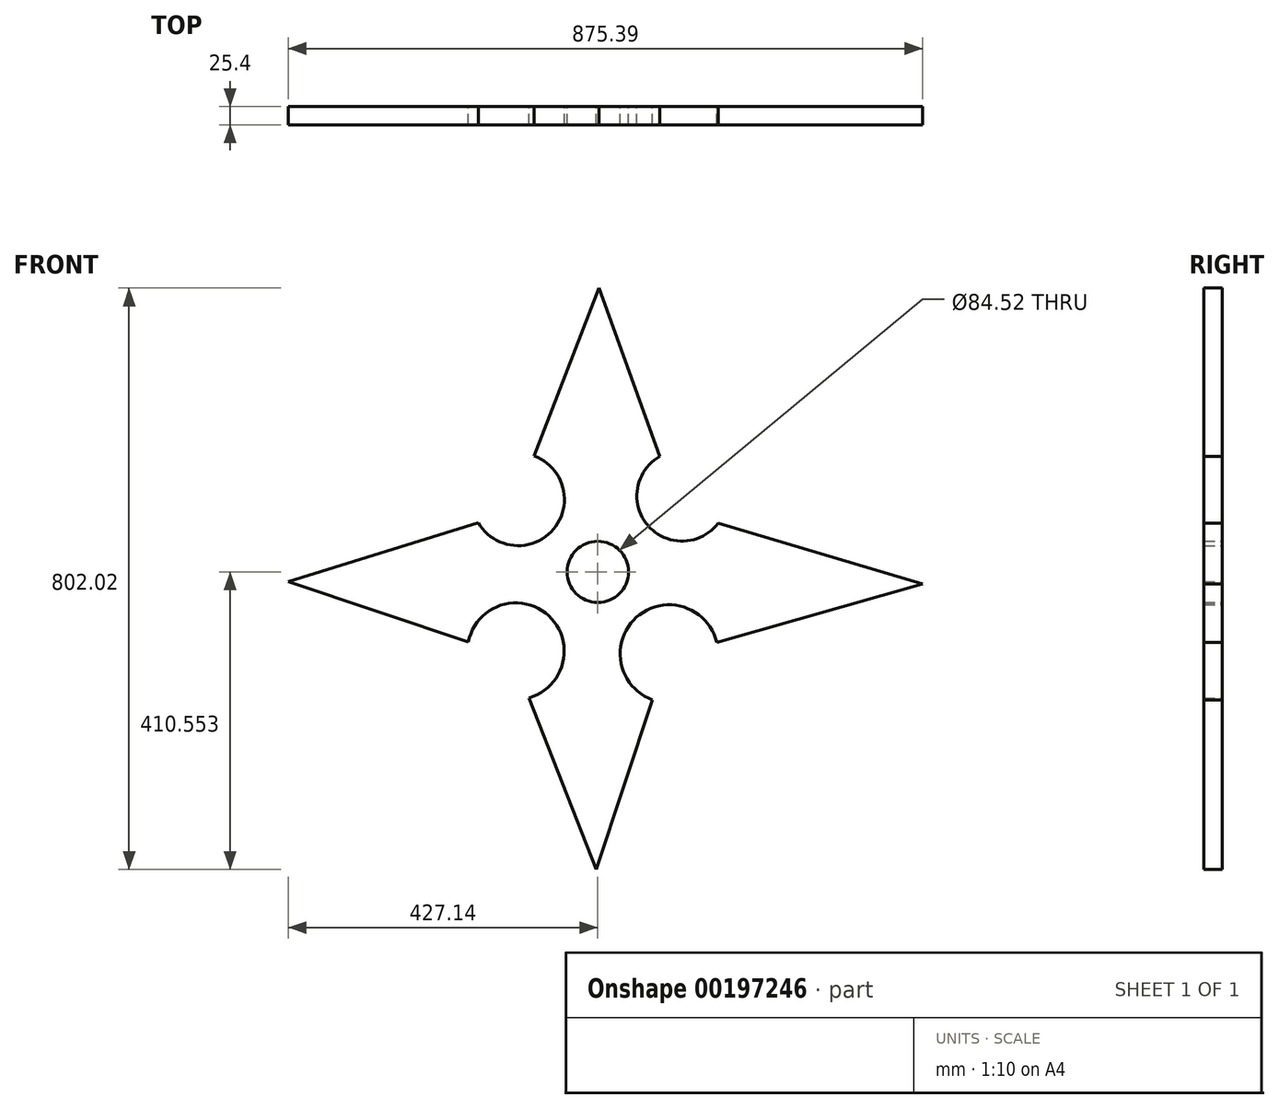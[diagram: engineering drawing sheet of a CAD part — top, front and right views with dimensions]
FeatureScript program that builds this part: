
annotation { "Feature Type Name" : "Feature", "Feature Type Description" : "" }
export const myFeature = defineFeature(function(context is Context, id is Id, definition is map)
    precondition{}
    {
        {
            var Q0;
            Q0=qCreatedBy(makeId("Front.planeOp"),FACE);
            var sketch = newSketch(context, id + "F0", { "sketchPlane" : qUnion([Q0])});
            skLineSegment(sketch, "E0", {"start": v(29.66, 76.77) * mm, "end": v(119.17, 308.51) * mm});
            skLineSegment(sketch, "E1", {"start": v(119.17, 308.51) * mm, "end": v(202.9, 76.26) * mm});
            skLineSegment(sketch, "E2", {"start": v(-47.67, -14.87) * mm, "end": v(-309.84, -96.66) * mm});
            skLineSegment(sketch, "E3", {"start": v(-309.84, -96.66) * mm, "end": v(-61.25, -179.52) * mm});
            skLineSegment(sketch, "E4", {"start": v(22.23, -256.74) * mm, "end": v(119.17, -504.48) * mm});
            skLineSegment(sketch, "E5", {"start": v(111.22, -504.48) * mm, "end": v(192.9, -259.48) * mm});
            skLineSegment(sketch, "E6", {"start": v(281.45, -180.33) * mm, "end": v(574.65, -96.66) * mm});
            skLineSegment(sketch, "E7", {"start": v(574.65, -101.95) * mm, "end": v(283.35, -15.69) * mm});
            skPoint(sketch, "E8", {"position": v(283.35, 59.58) * mm});
            skArc(sketch, "E9", {"start": v(202.9, 76.26) * mm, "mid": v(186.65, -19.13) * mm, "end": v(283.35, -15.69) * mm});
            skPoint(sketch, "E9.second.point", {"position": v(195.96, -27.8) * mm});
            skPoint(sketch, "E9.third.point", {"position": v(283.35, -15.69) * mm});
            skPoint(sketch, "E10.orphan", {"position": v(230.4, 0) * mm});
            skPoint(sketch, "E11", {"position": v(-50.32, 43.7) * mm});
            skArc(sketch, "E12", {"start": v(-47.67, -14.87) * mm, "mid": v(56.3, -24.15) * mm, "end": v(29.66, 76.77) * mm});
            skPoint(sketch, "E12.second.point", {"position": v(52.96, -27.8) * mm});
            skPoint(sketch, "E12.third.point", {"position": v(0, -46.34) * mm});
            skPoint(sketch, "E13.orphan", {"position": v(0, 0) * mm});
            skPoint(sketch, "E14", {"position": v(-29.13, -250.25) * mm});
            skArc(sketch, "E15", {"start": v(22.23, -256.74) * mm, "mid": v(49.61, -143.4) * mm, "end": v(-61.25, -179.52) * mm});
            skPoint(sketch, "E15.second.point", {"position": v(47.67, -141.68) * mm});
            skPoint(sketch, "E15.third.point", {"position": v(0, -125.79) * mm});
            skPoint(sketch, "E16", {"position": v(262.17, -244.96) * mm});
            skArc(sketch, "E17", {"start": v(281.45, -180.33) * mm, "mid": v(170.72, -145.55) * mm, "end": v(192.9, -259.48) * mm});
            skPoint(sketch, "E17.second.point", {"position": v(172.13, -144.33) * mm});
            skPoint(sketch, "E17.third.point", {"position": v(212.74, -128.44) * mm});
            skPoint(sketch, "E18.orphan", {"position": v(0, -199.94) * mm});
            skPoint(sketch, "E19.orphan", {"position": v(212.74, -199.94) * mm});
            skCircle(sketch, "E20", {"center": v(117.3, -82.96) * mm, "radius": 42.26 * mm});
            skPoint(sketch, "E20.first.point", {"position": v(82.1, -59.58) * mm});
            skPoint(sketch, "E20.second.point", {"position": v(153.6, -104.6) * mm});
            skPoint(sketch, "E20.third.point", {"position": v(158.9, -75.47) * mm});
            skSolve(sketch);
        }
        {
            var Q0;
            Q0=makeQuery(id+"F0.imprint","IMPRINT",FACE,{"disambiguationData":[TD([[makeQuery(id+"F0.imprint","IMPRINT",EDGE,{"derivedFrom":sQuery(id+"F0.wireOp",EDGE,"E0")}),-1.0]])]});
            extrude(context, id + "F1", {"entities" : qUnion([Q0]), "depth" : 12.7 * mm});
        }
        {
            var Q0;
            Q0=makeQuery(id+"F1.opExtrude","CAP_FACE",FACE,{"disambiguationData":[OSD([sQuery(id+"F0.wireOp",EDGE,"E0"),sQuery(id+"F0.wireOp",EDGE,"E1"),sQuery(id+"F0.wireOp",EDGE,"E2"),sQuery(id+"F0.wireOp",EDGE,"E3"),sQuery(id+"F0.wireOp",EDGE,"E4"),sQuery(id+"F0.wireOp",EDGE,"E5"),sQuery(id+"F0.wireOp",EDGE,"E6"),sQuery(id+"F0.wireOp",EDGE,"E7"),sQuery(id+"F0.wireOp",EDGE,"E9"),sQuery(id+"F0.wireOp",EDGE,"E12"),sQuery(id+"F0.wireOp",EDGE,"E15"),sQuery(id+"F0.wireOp",EDGE,"E17"),sQuery(id+"F0.wireOp",EDGE,"E20")])],"isStart":false});
            extrude(context, id + "F2", {"entities" : qUnion([Q0]), "operationType" : NewBodyOperationType.ADD, "depth" : 12.7 * mm});
        }
    });
